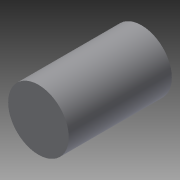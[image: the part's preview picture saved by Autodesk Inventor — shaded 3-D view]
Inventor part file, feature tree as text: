
AUTODESK INVENTOR PART (.ipt)
format: ipt  version: 2015 (Build 190159000, 159)  size: 79,360 bytes
history: native  units: mm
features: extrude x1, shell x1, sketch x1
ambient origin geometry x8: Origin, YZ Plane, XZ Plane, XY Plane, X Axis, Y Axis, Z Axis, Center Point
bodies: Solid1 (feature_tree)
feature tree (3):
  extrude  "Extrusion1"  Depth=125.0mm TaperAngle=0.0deg
  shell  "Shell1"  Thickness=3.0mm
  sketch  "Sketch1"  dims[d0=73.5mm d1=125.0mm d2=0.0mm d3=3.0mm]
